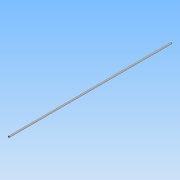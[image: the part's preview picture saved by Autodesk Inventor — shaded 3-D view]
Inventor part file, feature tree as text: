
AUTODESK INVENTOR PART (.ipt)
format: ipt  version: 2015 (Build 190159000, 159)  size: 64,512 bytes
history: native  units: mm
features: extrude x1, sketch x1
ambient origin geometry x8: Origin, YZ Plane, XZ Plane, XY Plane, X Axis, Y Axis, Z Axis, Center Point
bodies: Solid1 (feature_tree)
feature tree (2):
  extrude  "Extrusion1"  Depth=560.0mm TaperAngle=0.0deg
  sketch  "Sketch1"  dims[d0=5.0mm d1=560.0mm d2=0.0mm]
